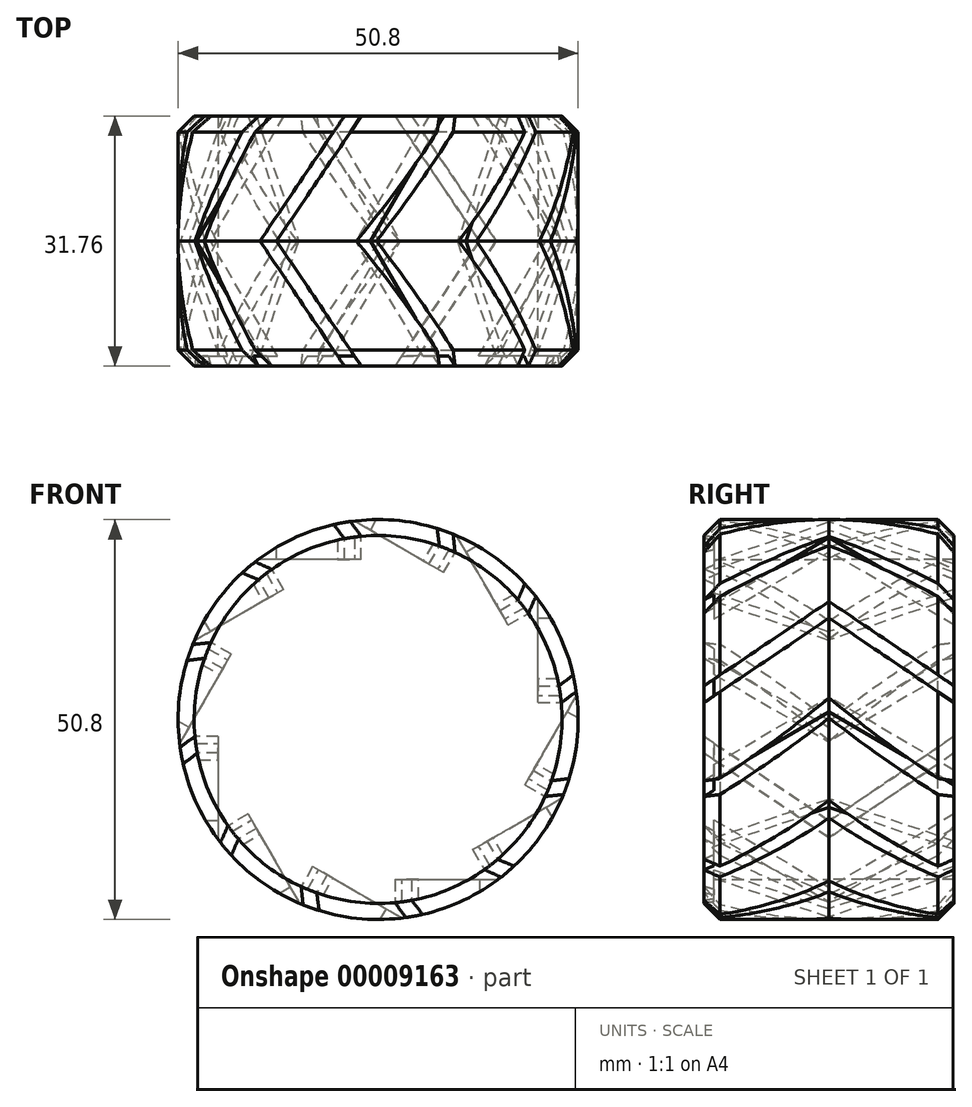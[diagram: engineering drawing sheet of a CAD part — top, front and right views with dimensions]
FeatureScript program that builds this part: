
annotation { "Feature Type Name" : "Feature", "Feature Type Description" : "" }
export const myFeature = defineFeature(function(context is Context, id is Id, definition is map)
    precondition{}
    {
        {
            var Q0;
            Q0=qCreatedBy(makeId("Front.planeOp"),FACE);
            var sketch = newSketch(context, id + "F0", { "sketchPlane" : qUnion([Q0])});
            skCircle(sketch, "E0", {"center": v(0, 0) * mm, "radius": 25.4 * mm});
            skSolve(sketch);
        }
        {
            var Q0;
            Q0=qSketchRegion(id+"F0",true);
            extrude(context, id + "F1", {"entities" : qUnion([Q0]), "depth" : 15.88 * mm});
        }
        {
            var Q0;
            Q0=qCreatedBy(makeId("Top.planeOp"),FACE);
            cPlane(context, id + "F2", {"entities" : qUnion([Q0]), "cplaneType" : CPlaneType.OFFSET, "offset" : 25.4 * mm, "width" : 152.4 * mm, "height" : 152.4 * mm});
        }
        {
            var Q0;
            Q0=qCreatedBy(id+"F2.planeOp",FACE);
            var sketch = newSketch(context, id + "F3", { "sketchPlane" : qUnion([Q0])});
            skLineSegment(sketch, "E1", {"start": v(0, 0) * mm, "end": v(0, -38.1) * mm});
            skLineSegment(sketch, "E2", {"start": v(0, -19.05) * mm, "end": v(-12.88, 0) * mm});
            skLineSegment(sketch, "E3", {"start": v(-12.88, 0) * mm, "end": v(15.76, -42.37) * mm});
            skLineSegment(sketch, "E4", {"start": v(15.76, -42.37) * mm, "end": v(13.63, -42.37) * mm});
            skLineSegment(sketch, "E5", {"start": v(13.63, -42.37) * mm, "end": v(-15, 0) * mm});
            skLineSegment(sketch, "E6", {"start": v(-15, 0) * mm, "end": v(-16.15, 1.8) * mm});
            skLineSegment(sketch, "E7", {"start": v(-16.15, 1.8) * mm, "end": v(-13.3, 1.8) * mm});
            skLineSegment(sketch, "E8", {"start": v(-13.3, 1.8) * mm, "end": v(-12.88, 0) * mm});
            skSolve(sketch);
        }
        {
            var Q0;
            Q0=qSketchRegion(id+"F3",true);
            extrude(context, id + "F4", {"entities" : qUnion([Q0]), "oppositeDirection" : true, "depth" : 5.08 * mm});
        }
        {
            var Q0;
            Q0=makeQuery(id+"F4.opExtrude","SWEPT_BODY",BODY,{"disambiguationData":[OSD([sQuery(id+"F3.wireOp",EDGE,"E3"),sQuery(id+"F3.wireOp",EDGE,"E4"),sQuery(id+"F3.wireOp",EDGE,"E5"),sQuery(id+"F3.wireOp",EDGE,"E6"),sQuery(id+"F3.wireOp",EDGE,"E7"),sQuery(id+"F3.wireOp",EDGE,"E8")])]});
            var Q1;
            Q1=makeQuery(id+"F1.opExtrude","CAP_EDGE",EDGE,{"disambiguationData":[OSD([sQuery(id+"F0.wireOp",EDGE,"E0")])],"isStart":false});
            circularPattern(context, id + "F5", {"entities" : qUnion([Q0]), "axis" : qUnion([Q1]), "angle" : 30 * degree, "instanceCount" : round(20)});
        }
        {
            var Q0;
            Q0=makeQuery(id+"F5.opPattern","COPY",BODY,{"derivedFrom":makeQuery(id+"F4.opExtrude","SWEPT_BODY",BODY,{"disambiguationData":[OSD([sQuery(id+"F3.wireOp",EDGE,"E3"),sQuery(id+"F3.wireOp",EDGE,"E4"),sQuery(id+"F3.wireOp",EDGE,"E5"),sQuery(id+"F3.wireOp",EDGE,"E6"),sQuery(id+"F3.wireOp",EDGE,"E7"),sQuery(id+"F3.wireOp",EDGE,"E8")])]}),"instanceName":"1"});
            var Q1;
            Q1=makeQuery(id+"F5.opPattern","COPY",BODY,{"derivedFrom":makeQuery(id+"F4.opExtrude","SWEPT_BODY",BODY,{"disambiguationData":[OSD([sQuery(id+"F3.wireOp",EDGE,"E3"),sQuery(id+"F3.wireOp",EDGE,"E4"),sQuery(id+"F3.wireOp",EDGE,"E5"),sQuery(id+"F3.wireOp",EDGE,"E6"),sQuery(id+"F3.wireOp",EDGE,"E7"),sQuery(id+"F3.wireOp",EDGE,"E8")])]}),"instanceName":"14"});
            var Q2;
            Q2=makeQuery(id+"F5.opPattern","COPY",BODY,{"derivedFrom":makeQuery(id+"F4.opExtrude","SWEPT_BODY",BODY,{"disambiguationData":[OSD([sQuery(id+"F3.wireOp",EDGE,"E3"),sQuery(id+"F3.wireOp",EDGE,"E4"),sQuery(id+"F3.wireOp",EDGE,"E5"),sQuery(id+"F3.wireOp",EDGE,"E6"),sQuery(id+"F3.wireOp",EDGE,"E7"),sQuery(id+"F3.wireOp",EDGE,"E8")])]}),"instanceName":"3"});
            var Q3;
            Q3=makeQuery(id+"F4.opExtrude","SWEPT_BODY",BODY,{"disambiguationData":[OSD([sQuery(id+"F3.wireOp",EDGE,"E3"),sQuery(id+"F3.wireOp",EDGE,"E4"),sQuery(id+"F3.wireOp",EDGE,"E5"),sQuery(id+"F3.wireOp",EDGE,"E6"),sQuery(id+"F3.wireOp",EDGE,"E7"),sQuery(id+"F3.wireOp",EDGE,"E8")])]});
            var Q4;
            Q4=makeQuery(id+"F5.opPattern","COPY",BODY,{"derivedFrom":makeQuery(id+"F4.opExtrude","SWEPT_BODY",BODY,{"disambiguationData":[OSD([sQuery(id+"F3.wireOp",EDGE,"E3"),sQuery(id+"F3.wireOp",EDGE,"E4"),sQuery(id+"F3.wireOp",EDGE,"E5"),sQuery(id+"F3.wireOp",EDGE,"E6"),sQuery(id+"F3.wireOp",EDGE,"E7"),sQuery(id+"F3.wireOp",EDGE,"E8")])]}),"instanceName":"11"});
            var Q5;
            Q5=makeQuery(id+"F5.opPattern","COPY",BODY,{"derivedFrom":makeQuery(id+"F4.opExtrude","SWEPT_BODY",BODY,{"disambiguationData":[OSD([sQuery(id+"F3.wireOp",EDGE,"E3"),sQuery(id+"F3.wireOp",EDGE,"E4"),sQuery(id+"F3.wireOp",EDGE,"E5"),sQuery(id+"F3.wireOp",EDGE,"E6"),sQuery(id+"F3.wireOp",EDGE,"E7"),sQuery(id+"F3.wireOp",EDGE,"E8")])]}),"instanceName":"10"});
            var Q6;
            Q6=makeQuery(id+"F1.opExtrude","SWEPT_BODY",BODY,{"disambiguationData":[OSD([sQuery(id+"F0.wireOp",EDGE,"E0")])]});
            var Q7;
            Q7=makeQuery(id+"F5.opPattern","COPY",BODY,{"derivedFrom":makeQuery(id+"F4.opExtrude","SWEPT_BODY",BODY,{"disambiguationData":[OSD([sQuery(id+"F3.wireOp",EDGE,"E3"),sQuery(id+"F3.wireOp",EDGE,"E4"),sQuery(id+"F3.wireOp",EDGE,"E5"),sQuery(id+"F3.wireOp",EDGE,"E6"),sQuery(id+"F3.wireOp",EDGE,"E7"),sQuery(id+"F3.wireOp",EDGE,"E8")])]}),"instanceName":"9"});
            var Q8;
            Q8=makeQuery(id+"F5.opPattern","COPY",BODY,{"derivedFrom":makeQuery(id+"F4.opExtrude","SWEPT_BODY",BODY,{"disambiguationData":[OSD([sQuery(id+"F3.wireOp",EDGE,"E3"),sQuery(id+"F3.wireOp",EDGE,"E4"),sQuery(id+"F3.wireOp",EDGE,"E5"),sQuery(id+"F3.wireOp",EDGE,"E6"),sQuery(id+"F3.wireOp",EDGE,"E7"),sQuery(id+"F3.wireOp",EDGE,"E8")])]}),"instanceName":"8"});
            var Q9;
            Q9=makeQuery(id+"F5.opPattern","COPY",BODY,{"derivedFrom":makeQuery(id+"F4.opExtrude","SWEPT_BODY",BODY,{"disambiguationData":[OSD([sQuery(id+"F3.wireOp",EDGE,"E3"),sQuery(id+"F3.wireOp",EDGE,"E4"),sQuery(id+"F3.wireOp",EDGE,"E5"),sQuery(id+"F3.wireOp",EDGE,"E6"),sQuery(id+"F3.wireOp",EDGE,"E7"),sQuery(id+"F3.wireOp",EDGE,"E8")])]}),"instanceName":"19"});
            var Q10;
            Q10=makeQuery(id+"F5.opPattern","COPY",BODY,{"derivedFrom":makeQuery(id+"F4.opExtrude","SWEPT_BODY",BODY,{"disambiguationData":[OSD([sQuery(id+"F3.wireOp",EDGE,"E3"),sQuery(id+"F3.wireOp",EDGE,"E4"),sQuery(id+"F3.wireOp",EDGE,"E5"),sQuery(id+"F3.wireOp",EDGE,"E6"),sQuery(id+"F3.wireOp",EDGE,"E7"),sQuery(id+"F3.wireOp",EDGE,"E8")])]}),"instanceName":"6"});
            var Q11;
            Q11=makeQuery(id+"F5.opPattern","COPY",BODY,{"derivedFrom":makeQuery(id+"F4.opExtrude","SWEPT_BODY",BODY,{"disambiguationData":[OSD([sQuery(id+"F3.wireOp",EDGE,"E3"),sQuery(id+"F3.wireOp",EDGE,"E4"),sQuery(id+"F3.wireOp",EDGE,"E5"),sQuery(id+"F3.wireOp",EDGE,"E6"),sQuery(id+"F3.wireOp",EDGE,"E7"),sQuery(id+"F3.wireOp",EDGE,"E8")])]}),"instanceName":"17"});
            var Q12;
            Q12=makeQuery(id+"F5.opPattern","COPY",BODY,{"derivedFrom":makeQuery(id+"F4.opExtrude","SWEPT_BODY",BODY,{"disambiguationData":[OSD([sQuery(id+"F3.wireOp",EDGE,"E3"),sQuery(id+"F3.wireOp",EDGE,"E4"),sQuery(id+"F3.wireOp",EDGE,"E5"),sQuery(id+"F3.wireOp",EDGE,"E6"),sQuery(id+"F3.wireOp",EDGE,"E7"),sQuery(id+"F3.wireOp",EDGE,"E8")])]}),"instanceName":"16"});
            var Q13;
            Q13=makeQuery(id+"F5.opPattern","COPY",BODY,{"derivedFrom":makeQuery(id+"F4.opExtrude","SWEPT_BODY",BODY,{"disambiguationData":[OSD([sQuery(id+"F3.wireOp",EDGE,"E3"),sQuery(id+"F3.wireOp",EDGE,"E4"),sQuery(id+"F3.wireOp",EDGE,"E5"),sQuery(id+"F3.wireOp",EDGE,"E6"),sQuery(id+"F3.wireOp",EDGE,"E7"),sQuery(id+"F3.wireOp",EDGE,"E8")])]}),"instanceName":"15"});
            var Q14;
            Q14=makeQuery(id+"F5.opPattern","COPY",BODY,{"derivedFrom":makeQuery(id+"F4.opExtrude","SWEPT_BODY",BODY,{"disambiguationData":[OSD([sQuery(id+"F3.wireOp",EDGE,"E3"),sQuery(id+"F3.wireOp",EDGE,"E4"),sQuery(id+"F3.wireOp",EDGE,"E5"),sQuery(id+"F3.wireOp",EDGE,"E6"),sQuery(id+"F3.wireOp",EDGE,"E7"),sQuery(id+"F3.wireOp",EDGE,"E8")])]}),"instanceName":"2"});
            var Q15;
            Q15=makeQuery(id+"F5.opPattern","COPY",BODY,{"derivedFrom":makeQuery(id+"F4.opExtrude","SWEPT_BODY",BODY,{"disambiguationData":[OSD([sQuery(id+"F3.wireOp",EDGE,"E3"),sQuery(id+"F3.wireOp",EDGE,"E4"),sQuery(id+"F3.wireOp",EDGE,"E5"),sQuery(id+"F3.wireOp",EDGE,"E6"),sQuery(id+"F3.wireOp",EDGE,"E7"),sQuery(id+"F3.wireOp",EDGE,"E8")])]}),"instanceName":"13"});
            booleanBodies(context, id + "F6", {"operationType" : BooleanOperationType.SUBTRACTION, "tools" : qUnion([Q0, Q1, Q2, Q3, Q4, Q5]), "targets" : qUnion([Q6, Q7, Q8, Q9, Q10, Q11, Q12, Q13, Q14, Q15])});
        }
        {
            var Q0;
            Q0=makeQuery(id+"F5.opPattern","COPY",BODY,{"derivedFrom":makeQuery(id+"F4.opExtrude","SWEPT_BODY",BODY,{"disambiguationData":[OSD([sQuery(id+"F3.wireOp",EDGE,"E3"),sQuery(id+"F3.wireOp",EDGE,"E4"),sQuery(id+"F3.wireOp",EDGE,"E5"),sQuery(id+"F3.wireOp",EDGE,"E6"),sQuery(id+"F3.wireOp",EDGE,"E7"),sQuery(id+"F3.wireOp",EDGE,"E8")])]}),"instanceName":"12"});
            var Q1;
            Q1=makeQuery(id+"F1.opExtrude","SWEPT_BODY",BODY,{"disambiguationData":[OSD([sQuery(id+"F0.wireOp",EDGE,"E0")])]});
            booleanBodies(context, id + "F7", {"operationType" : BooleanOperationType.SUBTRACTION, "tools" : qUnion([Q0]), "targets" : qUnion([Q1])});
        }
        {
            var Q0;
            Q0=makeQuery(id+"F5.opPattern","COPY",BODY,{"derivedFrom":makeQuery(id+"F4.opExtrude","SWEPT_BODY",BODY,{"disambiguationData":[OSD([sQuery(id+"F3.wireOp",EDGE,"E3"),sQuery(id+"F3.wireOp",EDGE,"E4"),sQuery(id+"F3.wireOp",EDGE,"E5"),sQuery(id+"F3.wireOp",EDGE,"E6"),sQuery(id+"F3.wireOp",EDGE,"E7"),sQuery(id+"F3.wireOp",EDGE,"E8")])]}),"instanceName":"9"});
            var Q1;
            Q1=makeQuery(id+"F5.opPattern","COPY",BODY,{"derivedFrom":makeQuery(id+"F4.opExtrude","SWEPT_BODY",BODY,{"disambiguationData":[OSD([sQuery(id+"F3.wireOp",EDGE,"E3"),sQuery(id+"F3.wireOp",EDGE,"E4"),sQuery(id+"F3.wireOp",EDGE,"E5"),sQuery(id+"F3.wireOp",EDGE,"E6"),sQuery(id+"F3.wireOp",EDGE,"E7"),sQuery(id+"F3.wireOp",EDGE,"E8")])]}),"instanceName":"16"});
            var Q2;
            Q2=makeQuery(id+"F5.opPattern","COPY",BODY,{"derivedFrom":makeQuery(id+"F4.opExtrude","SWEPT_BODY",BODY,{"disambiguationData":[OSD([sQuery(id+"F3.wireOp",EDGE,"E3"),sQuery(id+"F3.wireOp",EDGE,"E4"),sQuery(id+"F3.wireOp",EDGE,"E5"),sQuery(id+"F3.wireOp",EDGE,"E6"),sQuery(id+"F3.wireOp",EDGE,"E7"),sQuery(id+"F3.wireOp",EDGE,"E8")])]}),"instanceName":"5"});
            var Q3;
            Q3=makeQuery(id+"F1.opExtrude","SWEPT_BODY",BODY,{"disambiguationData":[OSD([sQuery(id+"F0.wireOp",EDGE,"E0")])]});
            booleanBodies(context, id + "F8", {"operationType" : BooleanOperationType.SUBTRACTION, "tools" : qUnion([Q0, Q1, Q2]), "targets" : qUnion([Q3])});
        }
        {
            var Q0;
            Q0=makeQuery(id+"F5.opPattern","COPY",BODY,{"derivedFrom":makeQuery(id+"F4.opExtrude","SWEPT_BODY",BODY,{"disambiguationData":[OSD([sQuery(id+"F3.wireOp",EDGE,"E3"),sQuery(id+"F3.wireOp",EDGE,"E4"),sQuery(id+"F3.wireOp",EDGE,"E5"),sQuery(id+"F3.wireOp",EDGE,"E6"),sQuery(id+"F3.wireOp",EDGE,"E7"),sQuery(id+"F3.wireOp",EDGE,"E8")])]}),"instanceName":"4"});
            var Q1;
            Q1=makeQuery(id+"F5.opPattern","COPY",BODY,{"derivedFrom":makeQuery(id+"F4.opExtrude","SWEPT_BODY",BODY,{"disambiguationData":[OSD([sQuery(id+"F3.wireOp",EDGE,"E3"),sQuery(id+"F3.wireOp",EDGE,"E4"),sQuery(id+"F3.wireOp",EDGE,"E5"),sQuery(id+"F3.wireOp",EDGE,"E6"),sQuery(id+"F3.wireOp",EDGE,"E7"),sQuery(id+"F3.wireOp",EDGE,"E8")])]}),"instanceName":"17"});
            var Q2;
            Q2=makeQuery(id+"F1.opExtrude","SWEPT_BODY",BODY,{"disambiguationData":[OSD([sQuery(id+"F0.wireOp",EDGE,"E0")])]});
            booleanBodies(context, id + "F9", {"operationType" : BooleanOperationType.SUBTRACTION, "tools" : qUnion([Q0, Q1]), "targets" : qUnion([Q2])});
        }
        {
            var Q0;
            Q0=makeQuery(id+"F5.opPattern","COPY",BODY,{"derivedFrom":makeQuery(id+"F4.opExtrude","SWEPT_BODY",BODY,{"disambiguationData":[OSD([sQuery(id+"F3.wireOp",EDGE,"E3"),sQuery(id+"F3.wireOp",EDGE,"E4"),sQuery(id+"F3.wireOp",EDGE,"E5"),sQuery(id+"F3.wireOp",EDGE,"E6"),sQuery(id+"F3.wireOp",EDGE,"E7"),sQuery(id+"F3.wireOp",EDGE,"E8")])]}),"instanceName":"6"});
            var Q1;
            Q1=makeQuery(id+"F5.opPattern","COPY",BODY,{"derivedFrom":makeQuery(id+"F4.opExtrude","SWEPT_BODY",BODY,{"disambiguationData":[OSD([sQuery(id+"F3.wireOp",EDGE,"E3"),sQuery(id+"F3.wireOp",EDGE,"E4"),sQuery(id+"F3.wireOp",EDGE,"E5"),sQuery(id+"F3.wireOp",EDGE,"E6"),sQuery(id+"F3.wireOp",EDGE,"E7"),sQuery(id+"F3.wireOp",EDGE,"E8")])]}),"instanceName":"19"});
            var Q2;
            Q2=makeQuery(id+"F5.opPattern","COPY",BODY,{"derivedFrom":makeQuery(id+"F4.opExtrude","SWEPT_BODY",BODY,{"disambiguationData":[OSD([sQuery(id+"F3.wireOp",EDGE,"E3"),sQuery(id+"F3.wireOp",EDGE,"E4"),sQuery(id+"F3.wireOp",EDGE,"E5"),sQuery(id+"F3.wireOp",EDGE,"E6"),sQuery(id+"F3.wireOp",EDGE,"E7"),sQuery(id+"F3.wireOp",EDGE,"E8")])]}),"instanceName":"8"});
            var Q3;
            Q3=makeQuery(id+"F1.opExtrude","SWEPT_BODY",BODY,{"disambiguationData":[OSD([sQuery(id+"F0.wireOp",EDGE,"E0")])]});
            booleanBodies(context, id + "F10", {"operationType" : BooleanOperationType.SUBTRACTION, "tools" : qUnion([Q0, Q1, Q2]), "targets" : qUnion([Q3])});
        }
        {
            var Q0;
            Q0=makeQuery(id+"F5.opPattern","COPY",BODY,{"derivedFrom":makeQuery(id+"F4.opExtrude","SWEPT_BODY",BODY,{"disambiguationData":[OSD([sQuery(id+"F3.wireOp",EDGE,"E3"),sQuery(id+"F3.wireOp",EDGE,"E4"),sQuery(id+"F3.wireOp",EDGE,"E5"),sQuery(id+"F3.wireOp",EDGE,"E6"),sQuery(id+"F3.wireOp",EDGE,"E7"),sQuery(id+"F3.wireOp",EDGE,"E8")])]}),"instanceName":"18"});
            var Q1;
            Q1=makeQuery(id+"F5.opPattern","COPY",BODY,{"derivedFrom":makeQuery(id+"F4.opExtrude","SWEPT_BODY",BODY,{"disambiguationData":[OSD([sQuery(id+"F3.wireOp",EDGE,"E3"),sQuery(id+"F3.wireOp",EDGE,"E4"),sQuery(id+"F3.wireOp",EDGE,"E5"),sQuery(id+"F3.wireOp",EDGE,"E6"),sQuery(id+"F3.wireOp",EDGE,"E7"),sQuery(id+"F3.wireOp",EDGE,"E8")])]}),"instanceName":"7"});
            var Q2;
            Q2=makeQuery(id+"F1.opExtrude","SWEPT_BODY",BODY,{"disambiguationData":[OSD([sQuery(id+"F0.wireOp",EDGE,"E0")])]});
            booleanBodies(context, id + "F11", {"operationType" : BooleanOperationType.SUBTRACTION, "tools" : qUnion([Q0, Q1]), "targets" : qUnion([Q2])});
        }
        {
            var Q0;
            Q0=makeQuery(id+"F1.opExtrude","SWEPT_BODY",BODY,{"disambiguationData":[OSD([sQuery(id+"F0.wireOp",EDGE,"E0")])]});
            var Q1;
            Q1=qCreatedBy(makeId("Front.planeOp"),FACE);
            mirror(context, id + "F12", {"entities" : qUnion([Q0]), "mirrorPlane" : qUnion([Q1])});
        }
        {
            var Q0;
            {var subQ0=sQuery(id+"F0.wireOp",EDGE,"E0");Q0=makeQuery(id+"F12.opPattern","COPY",EDGE,{"derivedFrom":makeQuery(id+"F6.opBoolean","SPLIT",EDGE,{"disambiguationData":[TD([makeQuery(id+"F5.opPattern","COPY",FACE,{"derivedFrom":makeQuery(id+"F4.opExtrude","SWEPT_FACE",FACE,{"disambiguationData":[OSD([sQuery(id+"F3.wireOp",EDGE,"E5")])]}),"instanceName":"1"})])],"derivedFrom":makeQuery(id+"F1.opExtrude","CAP_EDGE",EDGE,{"disambiguationData":[OSD([subQ0])],"isStart":false})}),"instanceName":"1"});}
            var Q1;
            {var subQ0=sQuery(id+"F0.wireOp",EDGE,"E0");Q1=makeQuery(id+"F12.opPattern","COPY",EDGE,{"derivedFrom":makeQuery(id+"F6.opBoolean","SPLIT",EDGE,{"disambiguationData":[TD([makeQuery(id+"F5.opPattern","COPY",FACE,{"derivedFrom":makeQuery(id+"F4.opExtrude","SWEPT_FACE",FACE,{"disambiguationData":[OSD([sQuery(id+"F3.wireOp",EDGE,"E3")])]}),"instanceName":"3"})])],"derivedFrom":makeQuery(id+"F1.opExtrude","CAP_EDGE",EDGE,{"disambiguationData":[OSD([subQ0])],"isStart":false})}),"instanceName":"1"});}
            var Q2;
            {var subQ0=sQuery(id+"F0.wireOp",EDGE,"E0");var subQ1=makeQuery(id+"F4.opExtrude","SWEPT_FACE",FACE,{"disambiguationData":[OSD([sQuery(id+"F3.wireOp",EDGE,"E3")])]});var subQ2=makeQuery(id+"F5.opPattern","COPY",FACE,{"derivedFrom":makeQuery(id+"F4.opExtrude","SWEPT_FACE",FACE,{"disambiguationData":[OSD([sQuery(id+"F3.wireOp",EDGE,"E5")])]}),"instanceName":"3"});Q2=makeQuery(id+"F12.opPattern","COPY",EDGE,{"derivedFrom":makeQuery(id+"F8.opBoolean","SPLIT",EDGE,{"disambiguationData":[TD([makeQuery(id+"F5.opPattern","COPY",FACE,{"derivedFrom":subQ1,"instanceName":"16"})])],"derivedFrom":makeQuery(id+"F6.opBoolean","SPLIT",EDGE,{"disambiguationData":[TD([subQ2])],"derivedFrom":makeQuery(id+"F1.opExtrude","CAP_EDGE",EDGE,{"disambiguationData":[OSD([subQ0])],"isStart":false})})}),"instanceName":"1"});}
            var Q3;
            {var subQ0=sQuery(id+"F0.wireOp",EDGE,"E0");var subQ1=makeQuery(id+"F4.opExtrude","SWEPT_FACE",FACE,{"disambiguationData":[OSD([sQuery(id+"F3.wireOp",EDGE,"E3")])]});var subQ2=makeQuery(id+"F4.opExtrude","SWEPT_FACE",FACE,{"disambiguationData":[OSD([sQuery(id+"F3.wireOp",EDGE,"E5")])]});Q3=makeQuery(id+"F12.opPattern","COPY",EDGE,{"derivedFrom":makeQuery(id+"F8.opBoolean","SPLIT",EDGE,{"disambiguationData":[TD([makeQuery(id+"F5.opPattern","COPY",FACE,{"derivedFrom":subQ1,"instanceName":"5"})])],"derivedFrom":makeQuery(id+"F6.opBoolean","SPLIT",EDGE,{"disambiguationData":[TD([makeQuery(id+"F5.opPattern","COPY",FACE,{"derivedFrom":subQ2,"instanceName":"3"})])],"derivedFrom":makeQuery(id+"F1.opExtrude","CAP_EDGE",EDGE,{"disambiguationData":[OSD([subQ0])],"isStart":false})})}),"instanceName":"1"});}
            var Q4;
            {var subQ0=sQuery(id+"F0.wireOp",EDGE,"E0");var subQ1=makeQuery(id+"F4.opExtrude","SWEPT_FACE",FACE,{"disambiguationData":[OSD([sQuery(id+"F3.wireOp",EDGE,"E3")])]});var subQ2=makeQuery(id+"F4.opExtrude","SWEPT_FACE",FACE,{"disambiguationData":[OSD([sQuery(id+"F3.wireOp",EDGE,"E5")])]});var subQ5=makeQuery(id+"F5.opPattern","COPY",FACE,{"derivedFrom":subQ2,"instanceName":"5"});Q4=makeQuery(id+"F12.opPattern","COPY",EDGE,{"derivedFrom":makeQuery(id+"F10.opBoolean","SPLIT",EDGE,{"disambiguationData":[TD([makeQuery(id+"F5.opPattern","COPY",FACE,{"derivedFrom":subQ1,"instanceName":"6"})])],"derivedFrom":makeQuery(id+"F8.opBoolean","SPLIT",EDGE,{"disambiguationData":[TD([subQ5])],"derivedFrom":makeQuery(id+"F6.opBoolean","SPLIT",EDGE,{"disambiguationData":[TD([makeQuery(id+"F5.opPattern","COPY",FACE,{"derivedFrom":subQ2,"instanceName":"3"})])],"derivedFrom":makeQuery(id+"F1.opExtrude","CAP_EDGE",EDGE,{"disambiguationData":[OSD([subQ0])],"isStart":false})})})}),"instanceName":"1"});}
            var Q5;
            {var subQ0=sQuery(id+"F0.wireOp",EDGE,"E0");var subQ2=makeQuery(id+"F4.opExtrude","SWEPT_FACE",FACE,{"disambiguationData":[OSD([sQuery(id+"F3.wireOp",EDGE,"E5")])]});Q5=makeQuery(id+"F12.opPattern","COPY",EDGE,{"derivedFrom":makeQuery(id+"F10.opBoolean","SPLIT",EDGE,{"disambiguationData":[TD([makeQuery(id+"F5.opPattern","COPY",FACE,{"derivedFrom":subQ2,"instanceName":"6"})])],"derivedFrom":makeQuery(id+"F8.opBoolean","SPLIT",EDGE,{"disambiguationData":[TD([makeQuery(id+"F5.opPattern","COPY",FACE,{"derivedFrom":subQ2,"instanceName":"5"})])],"derivedFrom":makeQuery(id+"F6.opBoolean","SPLIT",EDGE,{"disambiguationData":[TD([makeQuery(id+"F5.opPattern","COPY",FACE,{"derivedFrom":subQ2,"instanceName":"3"})])],"derivedFrom":makeQuery(id+"F1.opExtrude","CAP_EDGE",EDGE,{"disambiguationData":[OSD([subQ0])],"isStart":false})})})}),"instanceName":"1"});}
            var Q6;
            {var subQ0=sQuery(id+"F0.wireOp",EDGE,"E0");var subQ1=makeQuery(id+"F4.opExtrude","SWEPT_FACE",FACE,{"disambiguationData":[OSD([sQuery(id+"F3.wireOp",EDGE,"E3")])]});var subQ2=makeQuery(id+"F4.opExtrude","SWEPT_FACE",FACE,{"disambiguationData":[OSD([sQuery(id+"F3.wireOp",EDGE,"E5")])]});Q6=makeQuery(id+"F12.opPattern","COPY",EDGE,{"derivedFrom":makeQuery(id+"F10.opBoolean","SPLIT",EDGE,{"disambiguationData":[TD([makeQuery(id+"F5.opPattern","COPY",FACE,{"derivedFrom":subQ1,"instanceName":"8"})])],"derivedFrom":makeQuery(id+"F8.opBoolean","SPLIT",EDGE,{"disambiguationData":[TD([makeQuery(id+"F5.opPattern","COPY",FACE,{"derivedFrom":subQ2,"instanceName":"5"})])],"derivedFrom":makeQuery(id+"F6.opBoolean","SPLIT",EDGE,{"disambiguationData":[TD([makeQuery(id+"F5.opPattern","COPY",FACE,{"derivedFrom":subQ2,"instanceName":"3"})])],"derivedFrom":makeQuery(id+"F1.opExtrude","CAP_EDGE",EDGE,{"disambiguationData":[OSD([subQ0])],"isStart":false})})})}),"instanceName":"1"});}
            var Q7;
            {var subQ0=sQuery(id+"F0.wireOp",EDGE,"E0");var subQ2=makeQuery(id+"F4.opExtrude","SWEPT_FACE",FACE,{"disambiguationData":[OSD([sQuery(id+"F3.wireOp",EDGE,"E5")])]});Q7=makeQuery(id+"F12.opPattern","COPY",EDGE,{"derivedFrom":makeQuery(id+"F10.opBoolean","SPLIT",EDGE,{"disambiguationData":[TD([makeQuery(id+"F5.opPattern","COPY",FACE,{"derivedFrom":subQ2,"instanceName":"8"})])],"derivedFrom":makeQuery(id+"F8.opBoolean","SPLIT",EDGE,{"disambiguationData":[TD([makeQuery(id+"F5.opPattern","COPY",FACE,{"derivedFrom":subQ2,"instanceName":"5"})])],"derivedFrom":makeQuery(id+"F6.opBoolean","SPLIT",EDGE,{"disambiguationData":[TD([makeQuery(id+"F5.opPattern","COPY",FACE,{"derivedFrom":subQ2,"instanceName":"3"})])],"derivedFrom":makeQuery(id+"F1.opExtrude","CAP_EDGE",EDGE,{"disambiguationData":[OSD([subQ0])],"isStart":false})})})}),"instanceName":"1"});}
            var Q8;
            {var subQ0=sQuery(id+"F0.wireOp",EDGE,"E0");var subQ2=makeQuery(id+"F4.opExtrude","SWEPT_FACE",FACE,{"disambiguationData":[OSD([sQuery(id+"F3.wireOp",EDGE,"E5")])]});Q8=makeQuery(id+"F12.opPattern","COPY",EDGE,{"derivedFrom":makeQuery(id+"F8.opBoolean","SPLIT",EDGE,{"disambiguationData":[TD([makeQuery(id+"F5.opPattern","COPY",FACE,{"derivedFrom":subQ2,"instanceName":"9"})])],"derivedFrom":makeQuery(id+"F6.opBoolean","SPLIT",EDGE,{"disambiguationData":[TD([makeQuery(id+"F5.opPattern","COPY",FACE,{"derivedFrom":subQ2,"instanceName":"3"})])],"derivedFrom":makeQuery(id+"F1.opExtrude","CAP_EDGE",EDGE,{"disambiguationData":[OSD([subQ0])],"isStart":false})})}),"instanceName":"1"});}
            var Q9;
            {var subQ0=sQuery(id+"F0.wireOp",EDGE,"E0");Q9=makeQuery(id+"F12.opPattern","COPY",EDGE,{"derivedFrom":makeQuery(id+"F6.opBoolean","SPLIT",EDGE,{"disambiguationData":[TD([makeQuery(id+"F5.opPattern","COPY",FACE,{"derivedFrom":makeQuery(id+"F4.opExtrude","SWEPT_FACE",FACE,{"disambiguationData":[OSD([sQuery(id+"F3.wireOp",EDGE,"E5")])]}),"instanceName":"10"})])],"derivedFrom":makeQuery(id+"F1.opExtrude","CAP_EDGE",EDGE,{"disambiguationData":[OSD([subQ0])],"isStart":false})}),"instanceName":"1"});}
            var Q10;
            {var subQ0=sQuery(id+"F0.wireOp",EDGE,"E0");Q10=makeQuery(id+"F12.opPattern","COPY",EDGE,{"derivedFrom":makeQuery(id+"F6.opBoolean","SPLIT",EDGE,{"disambiguationData":[TD([makeQuery(id+"F4.opExtrude","SWEPT_FACE",FACE,{"disambiguationData":[OSD([sQuery(id+"F3.wireOp",EDGE,"E3")])]})])],"derivedFrom":makeQuery(id+"F1.opExtrude","CAP_EDGE",EDGE,{"disambiguationData":[OSD([subQ0])],"isStart":false})}),"instanceName":"1"});}
            var Q11;
            {var subQ0=sQuery(id+"F0.wireOp",EDGE,"E0");Q11=makeQuery(id+"F12.opPattern","COPY",EDGE,{"derivedFrom":makeQuery(id+"F6.opBoolean","SPLIT",EDGE,{"disambiguationData":[TD([makeQuery(id+"F4.opExtrude","SWEPT_FACE",FACE,{"disambiguationData":[OSD([sQuery(id+"F3.wireOp",EDGE,"E5")])]})])],"derivedFrom":makeQuery(id+"F1.opExtrude","CAP_EDGE",EDGE,{"disambiguationData":[OSD([subQ0])],"isStart":false})}),"instanceName":"1"});}
            var Q12;
            {var subQ0=sQuery(id+"F0.wireOp",EDGE,"E0");Q12=makeQuery(id+"F6.opBoolean","SPLIT",EDGE,{"disambiguationData":[TD([makeQuery(id+"F5.opPattern","COPY",FACE,{"derivedFrom":makeQuery(id+"F4.opExtrude","SWEPT_FACE",FACE,{"disambiguationData":[OSD([sQuery(id+"F3.wireOp",EDGE,"E5")])]}),"instanceName":"1"})])],"derivedFrom":makeQuery(id+"F1.opExtrude","CAP_EDGE",EDGE,{"disambiguationData":[OSD([subQ0])],"isStart":false})});}
            var Q13;
            {var subQ0=sQuery(id+"F0.wireOp",EDGE,"E0");Q13=makeQuery(id+"F6.opBoolean","SPLIT",EDGE,{"disambiguationData":[TD([makeQuery(id+"F5.opPattern","COPY",FACE,{"derivedFrom":makeQuery(id+"F4.opExtrude","SWEPT_FACE",FACE,{"disambiguationData":[OSD([sQuery(id+"F3.wireOp",EDGE,"E3")])]}),"instanceName":"3"})])],"derivedFrom":makeQuery(id+"F1.opExtrude","CAP_EDGE",EDGE,{"disambiguationData":[OSD([subQ0])],"isStart":false})});}
            var Q14;
            {var subQ0=sQuery(id+"F0.wireOp",EDGE,"E0");var subQ1=makeQuery(id+"F4.opExtrude","SWEPT_FACE",FACE,{"disambiguationData":[OSD([sQuery(id+"F3.wireOp",EDGE,"E3")])]});var subQ2=makeQuery(id+"F5.opPattern","COPY",FACE,{"derivedFrom":makeQuery(id+"F4.opExtrude","SWEPT_FACE",FACE,{"disambiguationData":[OSD([sQuery(id+"F3.wireOp",EDGE,"E5")])]}),"instanceName":"3"});Q14=makeQuery(id+"F8.opBoolean","SPLIT",EDGE,{"disambiguationData":[TD([makeQuery(id+"F5.opPattern","COPY",FACE,{"derivedFrom":subQ1,"instanceName":"16"})])],"derivedFrom":makeQuery(id+"F6.opBoolean","SPLIT",EDGE,{"disambiguationData":[TD([subQ2])],"derivedFrom":makeQuery(id+"F1.opExtrude","CAP_EDGE",EDGE,{"disambiguationData":[OSD([subQ0])],"isStart":false})})});}
            var Q15;
            {var subQ0=sQuery(id+"F0.wireOp",EDGE,"E0");var subQ1=makeQuery(id+"F4.opExtrude","SWEPT_FACE",FACE,{"disambiguationData":[OSD([sQuery(id+"F3.wireOp",EDGE,"E3")])]});var subQ2=makeQuery(id+"F4.opExtrude","SWEPT_FACE",FACE,{"disambiguationData":[OSD([sQuery(id+"F3.wireOp",EDGE,"E5")])]});Q15=makeQuery(id+"F8.opBoolean","SPLIT",EDGE,{"disambiguationData":[TD([makeQuery(id+"F5.opPattern","COPY",FACE,{"derivedFrom":subQ1,"instanceName":"5"})])],"derivedFrom":makeQuery(id+"F6.opBoolean","SPLIT",EDGE,{"disambiguationData":[TD([makeQuery(id+"F5.opPattern","COPY",FACE,{"derivedFrom":subQ2,"instanceName":"3"})])],"derivedFrom":makeQuery(id+"F1.opExtrude","CAP_EDGE",EDGE,{"disambiguationData":[OSD([subQ0])],"isStart":false})})});}
            var Q16;
            {var subQ0=sQuery(id+"F0.wireOp",EDGE,"E0");Q16=makeQuery(id+"F6.opBoolean","SPLIT",EDGE,{"disambiguationData":[TD([makeQuery(id+"F4.opExtrude","SWEPT_FACE",FACE,{"disambiguationData":[OSD([sQuery(id+"F3.wireOp",EDGE,"E5")])]})])],"derivedFrom":makeQuery(id+"F1.opExtrude","CAP_EDGE",EDGE,{"disambiguationData":[OSD([subQ0])],"isStart":false})});}
            var Q17;
            {var subQ0=sQuery(id+"F0.wireOp",EDGE,"E0");var subQ1=makeQuery(id+"F4.opExtrude","SWEPT_FACE",FACE,{"disambiguationData":[OSD([sQuery(id+"F3.wireOp",EDGE,"E3")])]});var subQ2=makeQuery(id+"F4.opExtrude","SWEPT_FACE",FACE,{"disambiguationData":[OSD([sQuery(id+"F3.wireOp",EDGE,"E5")])]});var subQ5=makeQuery(id+"F5.opPattern","COPY",FACE,{"derivedFrom":subQ2,"instanceName":"5"});Q17=makeQuery(id+"F10.opBoolean","SPLIT",EDGE,{"disambiguationData":[TD([makeQuery(id+"F5.opPattern","COPY",FACE,{"derivedFrom":subQ1,"instanceName":"6"})])],"derivedFrom":makeQuery(id+"F8.opBoolean","SPLIT",EDGE,{"disambiguationData":[TD([subQ5])],"derivedFrom":makeQuery(id+"F6.opBoolean","SPLIT",EDGE,{"disambiguationData":[TD([makeQuery(id+"F5.opPattern","COPY",FACE,{"derivedFrom":subQ2,"instanceName":"3"})])],"derivedFrom":makeQuery(id+"F1.opExtrude","CAP_EDGE",EDGE,{"disambiguationData":[OSD([subQ0])],"isStart":false})})})});}
            var Q18;
            {var subQ0=sQuery(id+"F0.wireOp",EDGE,"E0");var subQ2=makeQuery(id+"F4.opExtrude","SWEPT_FACE",FACE,{"disambiguationData":[OSD([sQuery(id+"F3.wireOp",EDGE,"E5")])]});Q18=makeQuery(id+"F10.opBoolean","SPLIT",EDGE,{"disambiguationData":[TD([makeQuery(id+"F5.opPattern","COPY",FACE,{"derivedFrom":subQ2,"instanceName":"6"})])],"derivedFrom":makeQuery(id+"F8.opBoolean","SPLIT",EDGE,{"disambiguationData":[TD([makeQuery(id+"F5.opPattern","COPY",FACE,{"derivedFrom":subQ2,"instanceName":"5"})])],"derivedFrom":makeQuery(id+"F6.opBoolean","SPLIT",EDGE,{"disambiguationData":[TD([makeQuery(id+"F5.opPattern","COPY",FACE,{"derivedFrom":subQ2,"instanceName":"3"})])],"derivedFrom":makeQuery(id+"F1.opExtrude","CAP_EDGE",EDGE,{"disambiguationData":[OSD([subQ0])],"isStart":false})})})});}
            var Q19;
            {var subQ0=sQuery(id+"F0.wireOp",EDGE,"E0");var subQ1=makeQuery(id+"F4.opExtrude","SWEPT_FACE",FACE,{"disambiguationData":[OSD([sQuery(id+"F3.wireOp",EDGE,"E3")])]});var subQ2=makeQuery(id+"F4.opExtrude","SWEPT_FACE",FACE,{"disambiguationData":[OSD([sQuery(id+"F3.wireOp",EDGE,"E5")])]});Q19=makeQuery(id+"F10.opBoolean","SPLIT",EDGE,{"disambiguationData":[TD([makeQuery(id+"F5.opPattern","COPY",FACE,{"derivedFrom":subQ1,"instanceName":"8"})])],"derivedFrom":makeQuery(id+"F8.opBoolean","SPLIT",EDGE,{"disambiguationData":[TD([makeQuery(id+"F5.opPattern","COPY",FACE,{"derivedFrom":subQ2,"instanceName":"5"})])],"derivedFrom":makeQuery(id+"F6.opBoolean","SPLIT",EDGE,{"disambiguationData":[TD([makeQuery(id+"F5.opPattern","COPY",FACE,{"derivedFrom":subQ2,"instanceName":"3"})])],"derivedFrom":makeQuery(id+"F1.opExtrude","CAP_EDGE",EDGE,{"disambiguationData":[OSD([subQ0])],"isStart":false})})})});}
            var Q20;
            {var subQ0=sQuery(id+"F0.wireOp",EDGE,"E0");var subQ2=makeQuery(id+"F4.opExtrude","SWEPT_FACE",FACE,{"disambiguationData":[OSD([sQuery(id+"F3.wireOp",EDGE,"E5")])]});Q20=makeQuery(id+"F10.opBoolean","SPLIT",EDGE,{"disambiguationData":[TD([makeQuery(id+"F5.opPattern","COPY",FACE,{"derivedFrom":subQ2,"instanceName":"8"})])],"derivedFrom":makeQuery(id+"F8.opBoolean","SPLIT",EDGE,{"disambiguationData":[TD([makeQuery(id+"F5.opPattern","COPY",FACE,{"derivedFrom":subQ2,"instanceName":"5"})])],"derivedFrom":makeQuery(id+"F6.opBoolean","SPLIT",EDGE,{"disambiguationData":[TD([makeQuery(id+"F5.opPattern","COPY",FACE,{"derivedFrom":subQ2,"instanceName":"3"})])],"derivedFrom":makeQuery(id+"F1.opExtrude","CAP_EDGE",EDGE,{"disambiguationData":[OSD([subQ0])],"isStart":false})})})});}
            var Q21;
            {var subQ0=sQuery(id+"F0.wireOp",EDGE,"E0");var subQ2=makeQuery(id+"F4.opExtrude","SWEPT_FACE",FACE,{"disambiguationData":[OSD([sQuery(id+"F3.wireOp",EDGE,"E5")])]});Q21=makeQuery(id+"F8.opBoolean","SPLIT",EDGE,{"disambiguationData":[TD([makeQuery(id+"F5.opPattern","COPY",FACE,{"derivedFrom":subQ2,"instanceName":"9"})])],"derivedFrom":makeQuery(id+"F6.opBoolean","SPLIT",EDGE,{"disambiguationData":[TD([makeQuery(id+"F5.opPattern","COPY",FACE,{"derivedFrom":subQ2,"instanceName":"3"})])],"derivedFrom":makeQuery(id+"F1.opExtrude","CAP_EDGE",EDGE,{"disambiguationData":[OSD([subQ0])],"isStart":false})})});}
            var Q22;
            {var subQ0=sQuery(id+"F0.wireOp",EDGE,"E0");Q22=makeQuery(id+"F6.opBoolean","SPLIT",EDGE,{"disambiguationData":[TD([makeQuery(id+"F5.opPattern","COPY",FACE,{"derivedFrom":makeQuery(id+"F4.opExtrude","SWEPT_FACE",FACE,{"disambiguationData":[OSD([sQuery(id+"F3.wireOp",EDGE,"E5")])]}),"instanceName":"10"})])],"derivedFrom":makeQuery(id+"F1.opExtrude","CAP_EDGE",EDGE,{"disambiguationData":[OSD([subQ0])],"isStart":false})});}
            var Q23;
            {var subQ0=sQuery(id+"F0.wireOp",EDGE,"E0");Q23=makeQuery(id+"F6.opBoolean","SPLIT",EDGE,{"disambiguationData":[TD([makeQuery(id+"F4.opExtrude","SWEPT_FACE",FACE,{"disambiguationData":[OSD([sQuery(id+"F3.wireOp",EDGE,"E3")])]})])],"derivedFrom":makeQuery(id+"F1.opExtrude","CAP_EDGE",EDGE,{"disambiguationData":[OSD([subQ0])],"isStart":false})});}
            chamfer(context, id + "F13", {"entities" : qUnion([Q0, Q1, Q2, Q3, Q4, Q5, Q6, Q7, Q8, Q9, Q10, Q11, Q12, Q13, Q14, Q15, Q16, Q17, Q18, Q19, Q20, Q21, Q22, Q23]), "width" : 2.03 * mm, "tangentPropagation" : true});
        }
        {
            var Q0;
            Q0=makeQuery(id+"F1.opExtrude","CAP_FACE",FACE,{"disambiguationData":[OSD([sQuery(id+"F0.wireOp",EDGE,"E0")])],"isStart":false});
            var sketch = newSketch(context, id + "F14", { "sketchPlane" : qUnion([Q0])});
            skCircle(sketch, "E9", {"center": v(0, 0) * mm, "radius": 23.37 * mm});
            skSolve(sketch);
        }
        {
            var Q0;
            Q0 = qSketchRegion(id + "F14", true);
            extrude(context, id + "F15", {"entities" : qUnion([Q0]), "operationType" : NewBodyOperationType.ADD, "oppositeDirection" : true, "depth" : 1.27 * mm});
        }
    });
